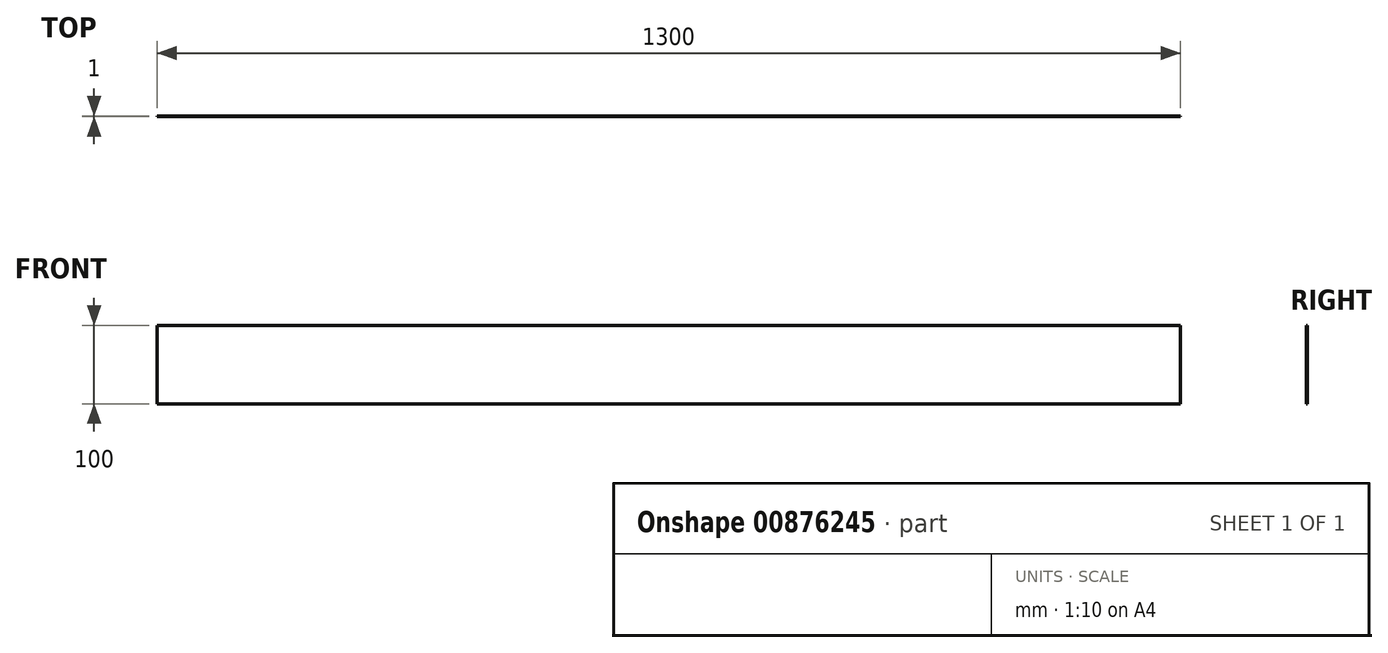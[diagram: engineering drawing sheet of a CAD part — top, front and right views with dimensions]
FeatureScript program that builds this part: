
annotation { "Feature Type Name" : "Feature", "Feature Type Description" : "" }
export const myFeature = defineFeature(function(context is Context, id is Id, definition is map)
    precondition{}
    {
        {
            var Q0;
            Q0=qCreatedBy(makeId("Front.planeOp"),FACE);
            var sketch = newSketch(context, id + "F0", { "sketchPlane" : qUnion([Q0])});
            skLineSegment(sketch, "E0.bottom", {"start": v(-650, 50) * mm, "end": v(650, 50) * mm});
            skLineSegment(sketch, "E0.top", {"start": v(-650, -50) * mm, "end": v(650, -50) * mm});
            skLineSegment(sketch, "E0.left", {"start": v(-650, 50) * mm, "end": v(-650, -50) * mm});
            skLineSegment(sketch, "E0.right", {"start": v(650, 50) * mm, "end": v(650, -50) * mm});
            skPoint(sketch, "E0.middle", {"position": v(0, 0) * mm});
            skSolve(sketch);
        }
        {
            var Q0;
            Q0=makeQuery(id+"F0.imprint","IMPRINT",FACE,{"disambiguationData":[TD([[makeQuery(id+"F0.imprint","IMPRINT",EDGE,{"derivedFrom":sQuery(id+"F0.wireOp",EDGE,"E0.bottom")}),-1.0]])]});
            extrude(context, id + "F1", {"entities" : qUnion([Q0]), "depth" : 1 * mm, "offsetDistance" : 25.4 * mm});
        }
    });
